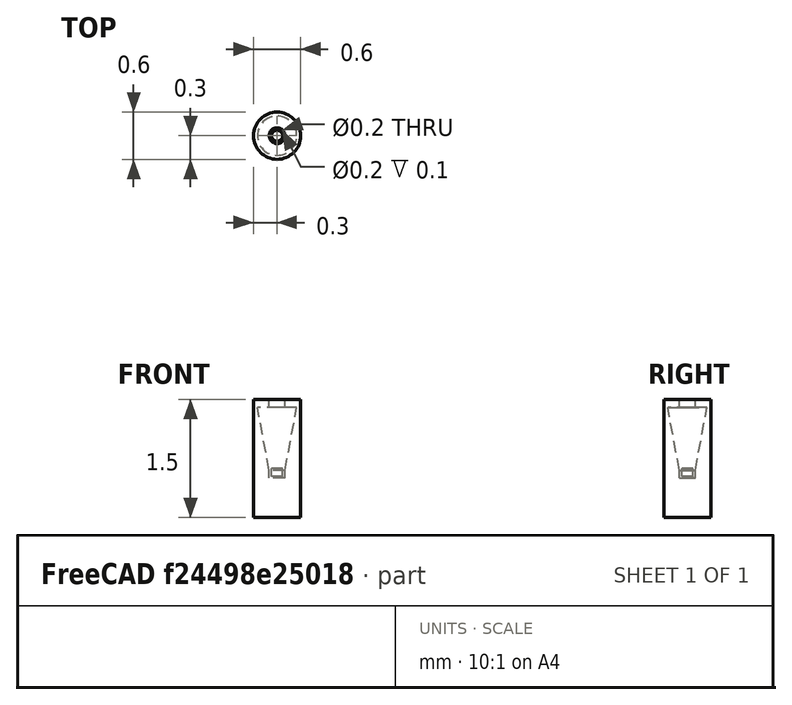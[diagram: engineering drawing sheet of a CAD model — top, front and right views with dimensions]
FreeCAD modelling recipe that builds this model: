
FCSTD DOCUMENT  (FreeCAD 0.17R13509 (Git))
Label: nozzle_test
License: All rights reserved
LicenseURL: http://en.wikipedia.org/wiki/All_rights_reserved
objects: Part::Cylinder×3, Part::Cone×1, Part::MultiFuse×1, Part::Cut×1
note: 6 computed .brp shape members not serialized (recipe doc carries the construction recipe); baked Part::Feature solids carry a one-line shape summary decoded from their .brp

FEATURE [Part::Cylinder] Cylinder
  Angle = 360
  AttacherType = Attacher::AttachEngine3D
  Height = 1.5
  Radius = 0.3
FEATURE [Part::Cylinder] Cylinder002  label="emitting_region"
  Angle = 360
  AttacherType = Attacher::AttachEngine3D
  Height = 0.1
  Placement = pos=(0,0,0.52) rot=(0,0,1;0rad)
  Radius = 0.07
FEATURE [Part::Cone] Cone
  Angle = 360
  AttacherType = Attacher::AttachEngine3D
  Height = 0.8
  Placement = pos=(0,0,0.6) rot=(0,0,1;0rad)
  Radius1 = 0.1
  Radius2 = 0.25
FEATURE [Part::Cylinder] Cylinder003  label="Cylinder001"
  Angle = 360
  AttacherType = Attacher::AttachEngine3D
  Height = 2
  Placement = pos=(0,0,0.5) rot=(0,0,1;0rad)
  Radius = 0.1
FEATURE [Part::MultiFuse] Fusion
  Shapes = -> [Cone,Cylinder003]
FEATURE [Part::Cut] Cut
  Base = -> Cylinder
  Tool = -> Fusion
